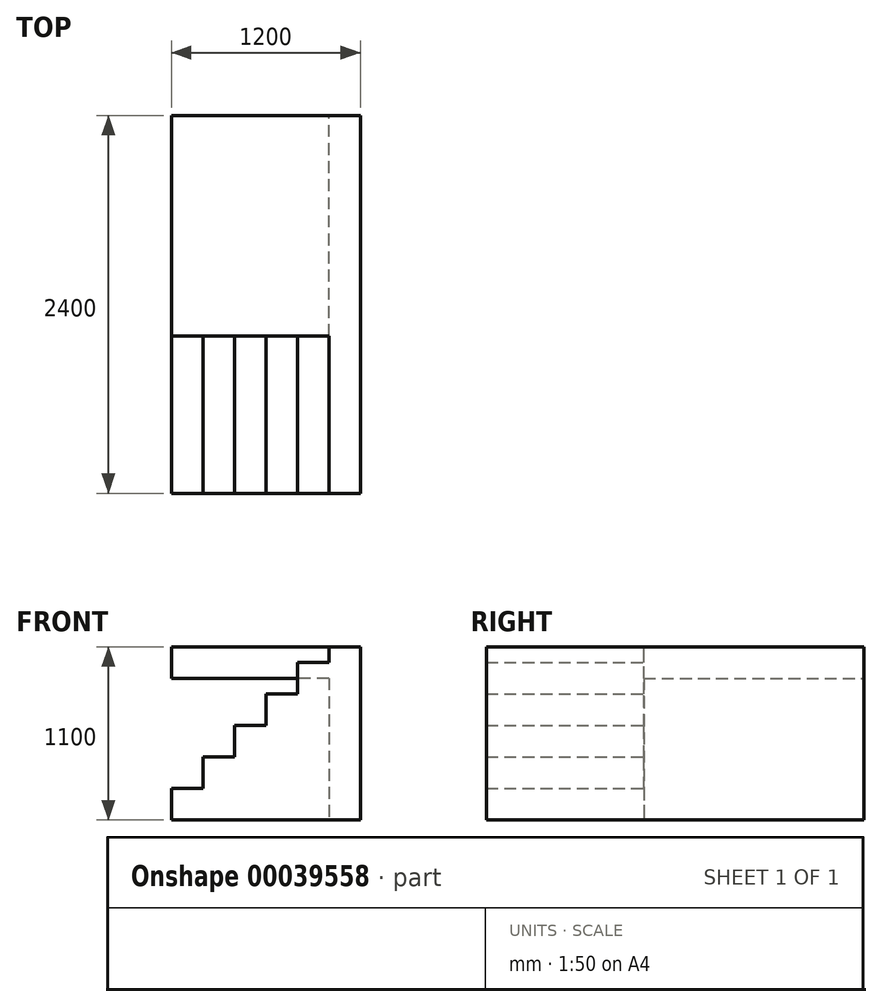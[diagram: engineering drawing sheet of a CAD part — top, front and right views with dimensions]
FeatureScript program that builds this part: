
annotation { "Feature Type Name" : "Feature", "Feature Type Description" : "" }
export const myFeature = defineFeature(function(context is Context, id is Id, definition is map)
    precondition{}
    {
        {
            var Q0;
            Q0=qCreatedBy(makeId("Front.planeOp"),FACE);
            var sketch = newSketch(context, id + "F0", { "sketchPlane" : qUnion([Q0])});
            skLineSegment(sketch, "E0", {"start": v(-154.34, 315.18) * mm, "end": v(-1154.34, 315.18) * mm});
            skLineSegment(sketch, "E1", {"start": v(-1154.34, 315.18) * mm, "end": v(-1154.34, 515.18) * mm});
            skLineSegment(sketch, "E2", {"start": v(-1154.34, 515.18) * mm, "end": v(45.66, 515.18) * mm});
            skLineSegment(sketch, "E3", {"start": v(45.66, 515.18) * mm, "end": v(45.66, -584.82) * mm});
            skLineSegment(sketch, "E4", {"start": v(45.66, -584.82) * mm, "end": v(-154.34, -584.82) * mm});
            skLineSegment(sketch, "E5", {"start": v(-154.34, -584.82) * mm, "end": v(-154.34, 315.18) * mm});
            skSolve(sketch);
        }
        {
            var Q0;
            Q0=makeQuery(id+"F0.imprint","IMPRINT",FACE,{"disambiguationData":[TD([[makeQuery(id+"F0.imprint","IMPRINT",EDGE,{"derivedFrom":sQuery(id+"F0.wireOp",EDGE,"E0")}),-1.0]])]});
            extrude(context, id + "F1", {"entities" : qUnion([Q0]), "depth" : 2400 * mm});
        }
        {
            var Q0;
            Q0=makeQuery(id+"F1.opExtrude","CAP_FACE",FACE,{"disambiguationData":[OSD([sQuery(id+"F0.wireOp",EDGE,"E0"),sQuery(id+"F0.wireOp",EDGE,"E1"),sQuery(id+"F0.wireOp",EDGE,"E2"),sQuery(id+"F0.wireOp",EDGE,"E3"),sQuery(id+"F0.wireOp",EDGE,"E4"),sQuery(id+"F0.wireOp",EDGE,"E5")])],"isStart":false});
            var sketch = newSketch(context, id + "F2", { "sketchPlane" : qUnion([Q0])});
            skLineSegment(sketch, "E6", {"start": v(-154.34, 315.18) * mm, "end": v(-154.34, 515.18) * mm});
            skSolve(sketch);
        }
        {
            var Q0;
            {var subQ1=sQuery(id+"F2.wireOp",EDGE,"E6");Q0=makeQuery(id+"F2.imprint","IMPRINT",FACE,{"disambiguationData":[TD([[makeQuery(id+"F2.imprint","IMPRINT",EDGE,{"derivedFrom":subQ1}),1.0]])]});}
            extrude(context, id + "F3", {"entities" : qUnion([Q0]), "operationType" : NewBodyOperationType.REMOVE, "oppositeDirection" : true, "depth" : 1000 * mm});
        }
        {
            var Q0;
            Q0=makeQuery(id+"F3.boolean.opBoolean","COPY",FACE,{"derivedFrom":makeQuery(id+"F3.opExtrude","CAP_FACE",FACE,{"disambiguationData":[OSD([sQuery(id+"F0.wireOp",EDGE,"E0"),sQuery(id+"F0.wireOp",EDGE,"E1"),sQuery(id+"F0.wireOp",EDGE,"E2"),sQuery(id+"F2.wireOp",EDGE,"E6")])],"isStart":false})});
            var sketch = newSketch(context, id + "F4", { "sketchPlane" : qUnion([Q0])});
            skLineSegment(sketch, "E7", {"start": v(-1154.34, 315.18) * mm, "end": v(-1154.34, -584.82) * mm});
            skLineSegment(sketch, "E8", {"start": v(-154.34, -584.82) * mm, "end": v(-1154.34, -584.82) * mm});
            skLineSegment(sketch, "E9", {"start": v(-1154.34, -584.82) * mm, "end": v(-1154.34, -384.82) * mm});
            skLineSegment(sketch, "E10", {"start": v(-1154.34, -384.82) * mm, "end": v(-954.34, -384.82) * mm});
            skLineSegment(sketch, "E11", {"start": v(-954.34, -384.82) * mm, "end": v(-954.34, -184.82) * mm});
            skLineSegment(sketch, "E12", {"start": v(-954.34, -184.82) * mm, "end": v(-754.34, -184.82) * mm});
            skLineSegment(sketch, "E13", {"start": v(-754.34, -184.82) * mm, "end": v(-754.34, 15.18) * mm});
            skLineSegment(sketch, "E14", {"start": v(-754.34, 15.18) * mm, "end": v(-554.34, 15.18) * mm});
            skLineSegment(sketch, "E15", {"start": v(-554.34, 15.18) * mm, "end": v(-554.34, 215.18) * mm});
            skLineSegment(sketch, "E16", {"start": v(-554.34, 215.18) * mm, "end": v(-354.34, 215.18) * mm});
            skLineSegment(sketch, "E17", {"start": v(-354.34, 215.18) * mm, "end": v(-354.34, 415.18) * mm});
            skLineSegment(sketch, "E18", {"start": v(-354.34, 415.18) * mm, "end": v(-154.34, 415.18) * mm});
            skLineSegment(sketch, "E19", {"start": v(-154.34, 415.18) * mm, "end": v(-154.34, -584.82) * mm});
            skPoint(sketch, "E20.orphan", {"position": v(-154.34, -873.2) * mm});
            skSolve(sketch);
        }
        {
            var Q0;
            Q0 = qSketchRegion(id + "F4", true);
            var Q1;
            {var subQ0=sQuery(id+"F4.wireOp",EDGE,"E8");Q1=makeQuery(id+"F4.imprint","IMPRINT",FACE,{"disambiguationData":[TD([[makeQuery(id+"F4.imprint","IMPRINT",EDGE,{"derivedFrom":subQ0}),-1.0]])]});}
            extrude(context, id + "F5", {"entities" : qUnion([Q0, Q1]), "operationType" : NewBodyOperationType.ADD, "depth" : 1000 * mm});
        }
    });
